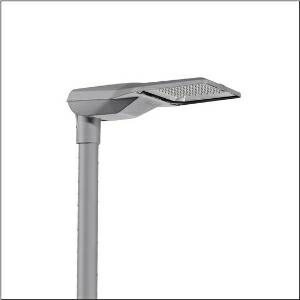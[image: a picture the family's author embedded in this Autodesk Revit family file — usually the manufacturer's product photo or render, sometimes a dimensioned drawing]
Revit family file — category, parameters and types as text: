
# Revit family: streetlight_sl_21_iq_midi___st1_0ab_5xe3m31d08mb_fee6
name_source: partatom
category: Lighting Fixtures
units: mm (PartAtom-declared; Revit-internal decimal feet)

## family parameters
Cut with Voids When Loaded = No
Host = Face
Light Source = No
Part Type = Normal
Room Calculation Point = No
Round Connector Dimension = Use Diameter
Shared = No

## types (1)
- --- (1 x LED, 17170 lm, 146.7 W, 3000K)
    Apparent Load = 147 VA
    CIE Flux Codes = 38 73 97 100 100
    Color Rendering = 70
    Color Temperature = 3000K
    Default Elevation = 1800 mm
    Description = Streetlight SL 21 iQ midi, mast luminaire, primary light control with lens, of PMMA, primary optical cover: cover, of toughened safety glass, transparent, light distribution: ST1.0aB, light emission: direct distribution, primary light characteristic: asymmetric, installation type: post-top, side-entry, LED, High Power LED, rated luminous flux: 17.170lm, luminous efficacy: 117lm/W, light colour: 730, colour temperature: 3000K, control gear: iQ-Comfort, control: Auto-Match, Temp-Guard, Lumen-Switch, Night-Set, Smart-Wire, Light-Fading, Desk-Remote (wireless, voltage-free reading and setting of iQ features in the workshop via application-optimized NFC function/RFID function), optimised constant luminous flux control (CLO 2.0), pre-setting: linear dimming characteristic, mains connection: 230..240V, AC, 50/60Hz, start of lifetime: 147W, end of service life: 161W, reduction: 62W, luminaire housing, of diecast aluminium, powder-coated, SITECO metallic grey (DB 702S), corrosivity category C5 high according to DIN EN ISO 12944, please order mast flange separately, inclination adjustable: 0°, 5°, 10°, 15°, sealing non-destructively replaceable, multi-level sealing system, length: 644mm, width: 335mm, height: 110mm, mast flange for spigot size: 42mm (side-entry): 5XC10008XM4, 60/48mm (side-entry/post-top): 5XC10108XM2, 76/60mm (side-entry/post-top): 5XC10108XM1, mounting height: 4..8m, protection rating (complete): IP66, insulation class (complete): insulation class II (safety insulation), certification: CE, ENEC, ENEC+, VDE, impact resistance: IK10, permissible operating ambient temperature for outdoor applications: -40..+50°C, standard-compliant lighting for roads and squares, packaging unit: 1 piece

Light Distribution: ST1.0aB
    Height = 111 mm
    Lamp = 1 x LED
    Lamp Light Flux = 17170 lm
    Lamp Power = 146.7 W
    Lamp count = 1
    Length = 644 mm
    Luminous efficacy = 117 lm/W
    Manufacturer = Siteco
    ModVariant = No
    Model = 5XE3M31D08MB
    Number of Poles = 1
    OnlyDefault = Yes
    Power Factor = 1
    Product Name = Streetlight SL 21 iQ midi | ST1.0aB
    Product group = mast luminaire | pylon top
    ProductGroupID = 6100
    Protection Class = Protection class II
    Protection Degree = IP 66
    RLX_Detail_Level = 1
    RLX_Emergency_Light_Flux = 0 lm
    RLX_Emergency_Type = 0
    RLX_Emergency_Type_DB = No
    RlxData = <blob elided: 26945 chars, md5=5f503df5>
    Socket = socket
    Standby Power = 0 W
    System Light Flux = 17170 lm
    System Power = 147 W
    Type Comments = factory setting: luminous flux: 100 % | dim-lin: 254 | 753 mA
    Type Image = l_1004298.jpg
    URL = http://relux.com
    VarID = @adj_180499
    Voltage = 0 V
    Weight = 0.00 kg
    Width = 336 mm

## geometry (parser evidence)
native form markers: Blend x4, Sweep x10
no freeform markers — native parametric forms only
